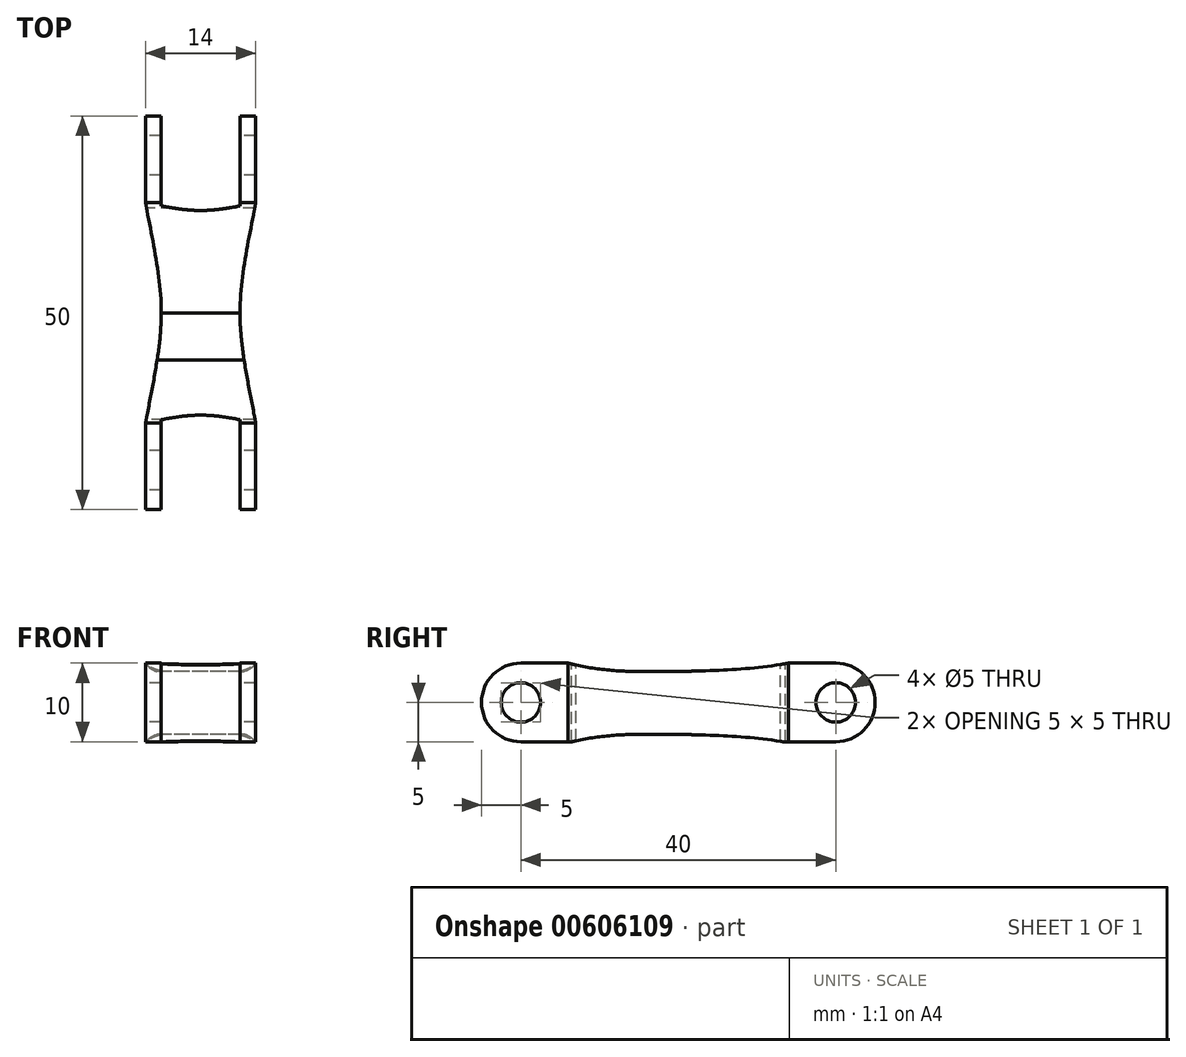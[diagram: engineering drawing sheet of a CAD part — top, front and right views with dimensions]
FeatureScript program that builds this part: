
annotation { "Feature Type Name" : "Feature", "Feature Type Description" : "" }
export const myFeature = defineFeature(function(context is Context, id is Id, definition is map)
    precondition{}
    {
        {
            var Q0;
            Q0=qCreatedBy(makeId("Right.planeOp"),FACE);
            var sketch = newSketch(context, id + "F0", { "sketchPlane" : qUnion([Q0])});
            skLineSegment(sketch, "E0.bottom", {"start": v(0, 0) * mm, "end": v(40, 0) * mm});
            skLineSegment(sketch, "E0.top", {"start": v(0, 10) * mm, "end": v(40, 10) * mm});
            skLineSegment(sketch, "E0.left", {"start": v(0, 0) * mm, "end": v(0, 10) * mm});
            skLineSegment(sketch, "E0.right", {"start": v(40, 0) * mm, "end": v(40, 10) * mm});
            skCircle(sketch, "E1", {"center": v(40, 5) * mm, "radius": 5 * mm});
            skCircle(sketch, "E2", {"center": v(40, 5) * mm, "radius": 2.5 * mm});
            skCircle(sketch, "E3", {"center": v(0, 5) * mm, "radius": 2.5 * mm});
            skCircle(sketch, "E4", {"center": v(0, 5) * mm, "radius": 5 * mm});
            skSolve(sketch);
        }
        {
            var Q0;
            Q0 = qSketchRegion(id + "F0", true);
            extrude(context, id + "F1", {"entities" : qUnion([Q0]), "depth" : 14 * mm, "offsetDistance" : 25.4 * mm});
        }
        {
            var Q0;
            Q0=makeQuery(id+"F1.opExtrude","SWEPT_FACE",FACE,{"disambiguationData":[OSD([sQuery(id+"F0.wireOp",EDGE,"E0.top")])]});
            var sketch = newSketch(context, id + "F2", { "sketchPlane" : qUnion([Q0])});
            skLineSegment(sketch, "E5.bottom", {"start": v(0, 34) * mm, "end": v(14, 34) * mm});
            skLineSegment(sketch, "E5.top", {"start": v(0, 6) * mm, "end": v(14, 6) * mm});
            skLineSegment(sketch, "E5.left", {"start": v(0, 34) * mm, "end": v(0, 6) * mm});
            skLineSegment(sketch, "E5.right", {"start": v(14, 34) * mm, "end": v(14, 6) * mm});
            skPoint(sketch, "E5.middle", {"position": v(7, 20) * mm});
            skPoint(sketch, "E5.middle.positionSnap0", {"position": v(7, 40) * mm});
            skPoint(sketch, "E5.centerSnap0", {"position": v(7, 40) * mm});
            skLineSegment(sketch, "E6.bottom", {"start": v(12, 50) * mm, "end": v(2, 50) * mm});
            skLineSegment(sketch, "E6.top", {"start": v(12, -10) * mm, "end": v(2, -10) * mm});
            skLineSegment(sketch, "E6.left", {"start": v(12, 50) * mm, "end": v(12, -10) * mm});
            skLineSegment(sketch, "E6.right", {"start": v(2, 50) * mm, "end": v(2, -10) * mm});
            skFitSpline(sketch, "E7", {"points": [v(14, 34) * mm, v(12, 20) * mm, v(14, 6) * mm], "startDerivative": vector(-6, -32) * mm, "endDerivative": vector(6, -32) * mm});
            skFitSpline(sketch, "E8", {"points": [v(0, 34) * mm, v(2, 20) * mm, v(0, 6) * mm], "startDerivative": vector(6, -32) * mm, "endDerivative": vector(-6, -32) * mm});
            skLineSegment(sketch, "E9", {"start": v(0, 33) * mm, "end": v(14, 33) * mm});
            skLineSegment(sketch, "E10", {"start": v(0, 7) * mm, "end": v(14, 7) * mm});
            skFitSpline(sketch, "E11", {"points": [v(0, 6) * mm, v(7, 7) * mm, v(14, 6) * mm], "startDerivative": vector(14, 3) * mm, "endDerivative": vector(14, -3) * mm});
            skFitSpline(sketch, "E12", {"points": [v(0, 34) * mm, v(7, 33) * mm, v(14, 34) * mm], "startDerivative": vector(14, -3) * mm, "endDerivative": vector(14, 3) * mm});
            skSolve(sketch);
        }
        {
            var Q0;
            {var subQ1=sQuery(id+"F2.wireOp",EDGE,"E6.right");var subQ4=sQuery(id+"F2.wireOp",EDGE,"E5.bottom");var subQ5=makeQuery(id+"F2.imprint","INTERSECT",VERTEX,{"derivedFrom":[subQ4,subQ1]});Q0=makeQuery(id+"F2.imprint","IMPRINT",FACE,{"disambiguationData":[TD([[makeQuery(id+"F2.imprint","IMPRINT",EDGE,{"disambiguationData":[TD([[subQ5,-1.0]])],"derivedFrom":subQ4}),-1.0]])]});}
            var Q1;
            {var subQ0=sQuery(id+"F2.wireOp",EDGE,"E6.right");var subQ1=sQuery(id+"F2.wireOp",EDGE,"E5.bottom");var subQ2=makeQuery(id+"F2.imprint","INTERSECT",VERTEX,{"derivedFrom":[subQ1,subQ0]});Q1=makeQuery(id+"F2.imprint","IMPRINT",FACE,{"disambiguationData":[TD([[makeQuery(id+"F2.imprint","IMPRINT",EDGE,{"disambiguationData":[TD([[subQ2,-1.0]])],"derivedFrom":subQ1}),1.0]])]});}
            var Q2;
            {var subQ0=sQuery(id+"F2.wireOp",EDGE,"E6.right");var subQ1=sQuery(id+"F2.wireOp",EDGE,"E5.top");var subQ2=makeQuery(id+"F2.imprint","INTERSECT",VERTEX,{"derivedFrom":[subQ1,subQ0]});Q2=makeQuery(id+"F2.imprint","IMPRINT",FACE,{"disambiguationData":[TD([[makeQuery(id+"F2.imprint","IMPRINT",EDGE,{"disambiguationData":[TD([[subQ2,-1.0]])],"derivedFrom":subQ1}),-1.0]])]});}
            var Q3;
            {var subQ1=sQuery(id+"F2.wireOp",EDGE,"E6.right");var subQ4=sQuery(id+"F2.wireOp",EDGE,"E5.top");var subQ5=makeQuery(id+"F2.imprint","INTERSECT",VERTEX,{"derivedFrom":[subQ4,subQ1]});Q3=makeQuery(id+"F2.imprint","IMPRINT",FACE,{"disambiguationData":[TD([[makeQuery(id+"F2.imprint","IMPRINT",EDGE,{"disambiguationData":[TD([[subQ5,-1.0]])],"derivedFrom":subQ4}),1.0]])]});}
            var Q4;
            {var subQ0=sQuery(id+"F2.wireOp",EDGE,"E6.top");Q4=makeQuery(id+"F2.imprint","IMPRINT",FACE,{"disambiguationData":[TD([[makeQuery(id+"F2.imprint","IMPRINT",EDGE,{"derivedFrom":subQ0}),-1.0]])]});}
            var Q5;
            {var subQ0=sQuery(id+"F2.wireOp",EDGE,"E9");var subQ1=sQuery(id+"F2.wireOp",EDGE,"E5.right");var subQ2=makeQuery(id+"F2.imprint","INTERSECT",VERTEX,{"derivedFrom":[subQ1,subQ0]});Q5=makeQuery(id+"F2.imprint","IMPRINT",FACE,{"disambiguationData":[TD([[makeQuery(id+"F2.imprint","IMPRINT",EDGE,{"disambiguationData":[TD([[subQ2,1.0]])],"derivedFrom":subQ1}),1.0]])]});}
            var Q6;
            {var subQ4=sQuery(id+"F2.wireOp",EDGE,"E9");var subQ5=sQuery(id+"F2.wireOp",EDGE,"E5.left");var subQ6=makeQuery(id+"F2.imprint","INTERSECT",VERTEX,{"derivedFrom":[subQ5,subQ4]});Q6=makeQuery(id+"F2.imprint","IMPRINT",FACE,{"disambiguationData":[TD([[makeQuery(id+"F2.imprint","IMPRINT",EDGE,{"disambiguationData":[TD([[subQ6,1.0]])],"derivedFrom":subQ5}),-1.0]])]});}
            var Q7;
            {var subQ0=sQuery(id+"F2.wireOp",EDGE,"E6.bottom");Q7=makeQuery(id+"F2.imprint","IMPRINT",FACE,{"disambiguationData":[TD([[makeQuery(id+"F2.imprint","IMPRINT",EDGE,{"derivedFrom":subQ0}),1.0]])]});}
            var Q8;
            {var subQ1=sQuery(id+"F2.wireOp",EDGE,"E5.left");var subQ3=sQuery(id+"F2.wireOp",EDGE,"E9");var subQ4=makeQuery(id+"F2.imprint","INTERSECT",VERTEX,{"derivedFrom":[subQ1,subQ3]});Q8=makeQuery(id+"F2.imprint","IMPRINT",FACE,{"disambiguationData":[TD([[makeQuery(id+"F2.imprint","IMPRINT",EDGE,{"disambiguationData":[TD([[subQ4,-1.0]])],"derivedFrom":subQ3}),1.0]])]});}
            var Q9;
            {var subQ1=sQuery(id+"F2.wireOp",EDGE,"E5.right");var subQ3=sQuery(id+"F2.wireOp",EDGE,"E9");var subQ4=makeQuery(id+"F2.imprint","INTERSECT",VERTEX,{"derivedFrom":[subQ1,subQ3]});Q9=makeQuery(id+"F2.imprint","IMPRINT",FACE,{"disambiguationData":[TD([[makeQuery(id+"F2.imprint","IMPRINT",EDGE,{"disambiguationData":[TD([[subQ4,1.0]])],"derivedFrom":subQ3}),1.0]])]});}
            var Q10;
            {var subQ1=sQuery(id+"F2.wireOp",EDGE,"E5.right");var subQ3=sQuery(id+"F2.wireOp",EDGE,"E10");var subQ4=makeQuery(id+"F2.imprint","INTERSECT",VERTEX,{"derivedFrom":[subQ1,subQ3]});Q10=makeQuery(id+"F2.imprint","IMPRINT",FACE,{"disambiguationData":[TD([[makeQuery(id+"F2.imprint","IMPRINT",EDGE,{"disambiguationData":[TD([[subQ4,1.0]])],"derivedFrom":subQ3}),-1.0]])]});}
            var Q11;
            {var subQ1=sQuery(id+"F2.wireOp",EDGE,"E5.left");var subQ3=sQuery(id+"F2.wireOp",EDGE,"E10");var subQ4=makeQuery(id+"F2.imprint","INTERSECT",VERTEX,{"derivedFrom":[subQ1,subQ3]});Q11=makeQuery(id+"F2.imprint","IMPRINT",FACE,{"disambiguationData":[TD([[makeQuery(id+"F2.imprint","IMPRINT",EDGE,{"disambiguationData":[TD([[subQ4,-1.0]])],"derivedFrom":subQ3}),-1.0]])]});}
            extrude(context, id + "F3", {"entities" : qUnion([Q0, Q1, Q2, Q3, Q4, Q5, Q6, Q7, Q8, Q9, Q10, Q11]), "operationType" : NewBodyOperationType.REMOVE, "oppositeDirection" : true, "depth" : 25.4 * mm, "offsetDistance" : 25.4 * mm});
        }
        {
            var Q0;
            Q0=qCreatedBy(makeId("Right.planeOp"),FACE);
            var sketch = newSketch(context, id + "F4", { "sketchPlane" : qUnion([Q0])});
            skLineSegment(sketch, "E13.bottom", {"start": v(6, 0.94) * mm, "end": v(34, 0.94) * mm});
            skLineSegment(sketch, "E13.top", {"start": v(6, 8.94) * mm, "end": v(34, 8.94) * mm});
            skLineSegment(sketch, "E13.left", {"start": v(6, 0.94) * mm, "end": v(6, 8.94) * mm});
            skLineSegment(sketch, "E13.right", {"start": v(34, 0.94) * mm, "end": v(34, 8.94) * mm});
            skPoint(sketch, "E13.middle", {"position": v(20, 4.94) * mm});
            skFitSpline(sketch, "E14", {"points": [v(6, 10) * mm, v(20, 8.94) * mm, v(34, 10) * mm], "startDerivative": vector(27.49, -7.25) * mm, "endDerivative": vector(28.35, 5.18) * mm});
            skLineSegment(sketch, "E15", {"start": v(20, 4.94) * mm, "end": v(45, 4.94) * mm, "construction": true});
            skPoint(sketch, "E15.endSnap0", {"position": v(34, 4.94) * mm});
            skFitSpline(sketch, "E16.MirrorCS", {"points": [v(6, -0.12) * mm, v(20, 0.94) * mm, v(34, -0.12) * mm], "startDerivative": vector(27.49, 7.25) * mm, "endDerivative": vector(28.35, -5.18) * mm});
            skLineSegment(sketch, "E17", {"start": v(34, 10) * mm, "end": v(6, 10) * mm});
            skLineSegment(sketch, "E18", {"start": v(34, -0.12) * mm, "end": v(6, -0.12) * mm});
            skSolve(sketch);
        }
        {
            var Q0;
            {var subQ4=sQuery(id+"F4.wireOp",EDGE,"E18");Q0=makeQuery(id+"F4.imprint","IMPRINT",FACE,{"disambiguationData":[TD([[makeQuery(id+"F4.imprint","IMPRINT",EDGE,{"derivedFrom":subQ4}),-1.0]])]});}
            var Q1;
            {var subQ4=sQuery(id+"F4.wireOp",EDGE,"E17");Q1=makeQuery(id+"F4.imprint","IMPRINT",FACE,{"disambiguationData":[TD([[makeQuery(id+"F4.imprint","IMPRINT",EDGE,{"derivedFrom":subQ4}),1.0]])]});}
            extrude(context, id + "F5", {"entities" : qUnion([Q0, Q1]), "operationType" : NewBodyOperationType.REMOVE, "depth" : 25.4 * mm, "offsetDistance" : 25.4 * mm});
        }
    });
